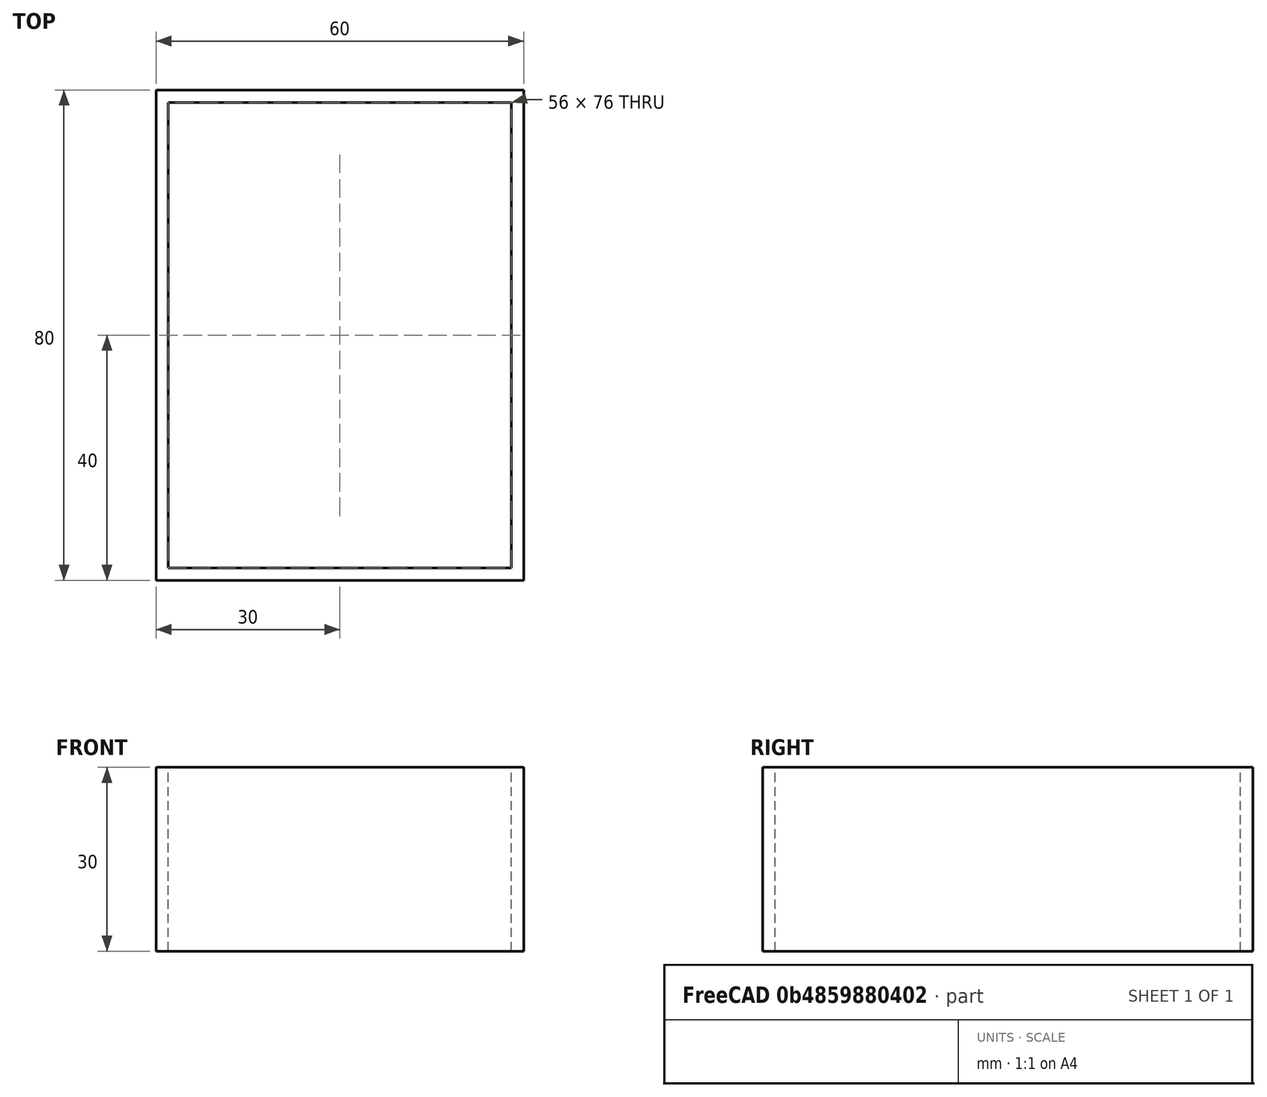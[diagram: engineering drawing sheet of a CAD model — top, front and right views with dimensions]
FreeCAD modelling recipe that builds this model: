
FCSTD DOCUMENT  (FreeCAD 0.15R4671 (Git))
Label: example 1
License: All rights reserved
LicenseURL: http://en.wikipedia.org/wiki/All_rights_reserved
objects: Sketcher::SketchObject×1, PartDesign::Pad×1
note: 3 computed .brp shape members not serialized (recipe doc carries the construction recipe); baked Part::Feature solids carry a one-line shape summary decoded from their .brp

FEATURE [Sketcher::SketchObject] Sketch001  label="sides sketch"
  Placement = pos=(0,0,2) rot=(0,0,1;0rad)
  sketch-geometry (8):
    g0: LineSegment StartX=-30 StartY=40 StartZ=0 EndX=30 EndY=40 EndZ=0
    g1: LineSegment StartX=30 StartY=40 StartZ=0 EndX=30 EndY=-40 EndZ=0
    g2: LineSegment StartX=30 StartY=-40 StartZ=0 EndX=-30 EndY=-40 EndZ=0
    g3: LineSegment StartX=-30 StartY=-40 StartZ=0 EndX=-30 EndY=40 EndZ=0
    g4: LineSegment StartX=-28 StartY=38 StartZ=0 EndX=28 EndY=38 EndZ=0
    g5: LineSegment StartX=28 StartY=38 StartZ=0 EndX=28 EndY=-38 EndZ=0
    g6: LineSegment StartX=28 StartY=-38 StartZ=0 EndX=-28 EndY=-38 EndZ=0
    g7: LineSegment StartX=-28 StartY=-38 StartZ=0 EndX=-28 EndY=38 EndZ=0
  constraints (24):
    c: Coincident(g0,g1)
    c: Coincident(g1,g2)
    c: Coincident(g2,g3)
    c: Coincident(g3,g0)
    c: Horizontal(g0)
    c: Horizontal(g2)
    c: Vertical(g1)
    c: Vertical(g3)
    c: Symmetric(g2,g1,g-2)
    c: Symmetric(g0,g2,g-1)
    c: DistanceY(g0,g2) = -80
    c: DistanceX(g2,g1) = 60
    c: Coincident(g4,g5)
    c: Coincident(g5,g6)
    c: Coincident(g6,g7)
    c: Coincident(g7,g4)
    c: Horizontal(g4)
    c: Horizontal(g6)
    c: Vertical(g5)
    c: Vertical(g7)
    c: DistanceX(g6,g2) = -2
    c: DistanceY(g6,g2) = -2
    c: DistanceY(g4,g0) = 2
    c: DistanceX(g4,g0) = 2
FEATURE [PartDesign::Pad] Pad  label="sides"
  Length = 30
  Length2 = 100
  Placement = pos=(0,0,2) rot=(0,0,1;0rad)
  Sketch = -> Sketch001
  Type = 0
